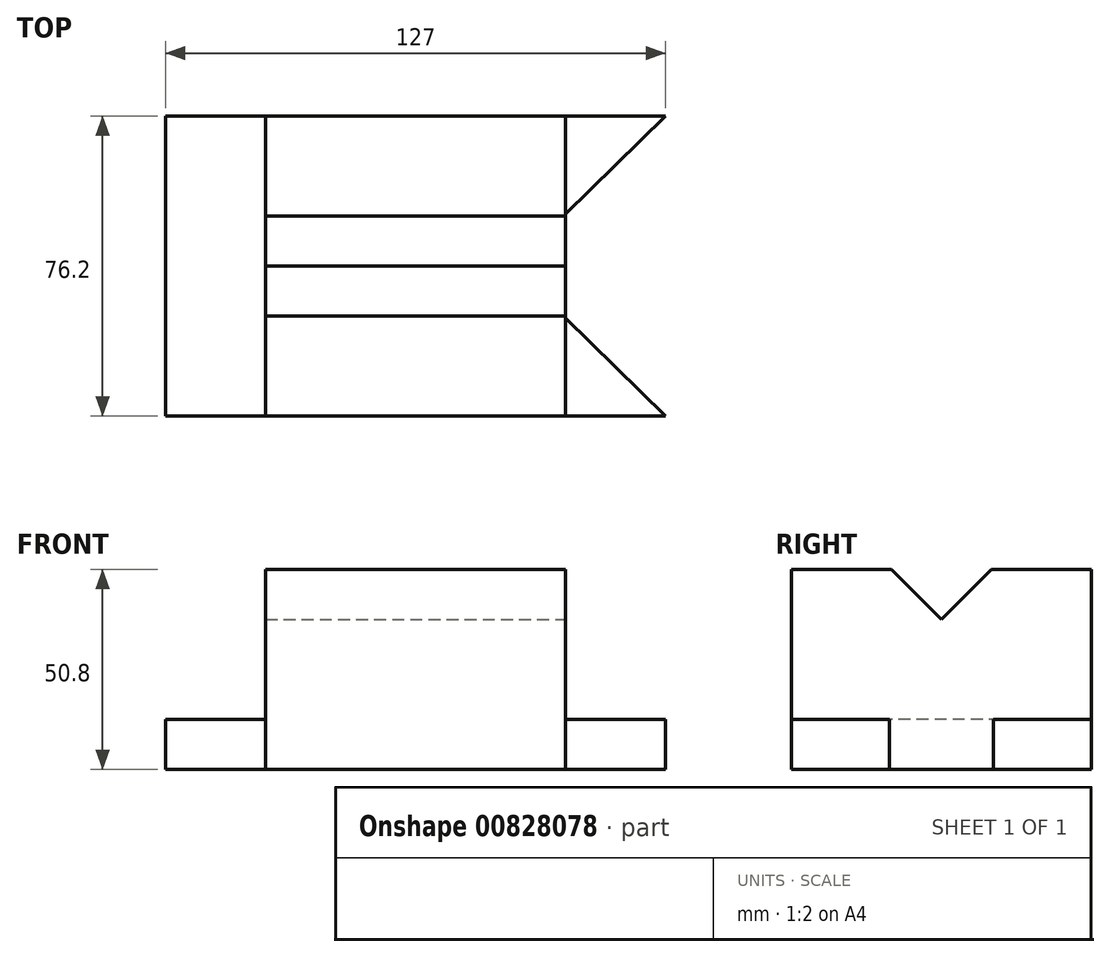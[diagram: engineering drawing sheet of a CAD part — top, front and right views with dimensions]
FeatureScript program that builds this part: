
annotation { "Feature Type Name" : "Feature", "Feature Type Description" : "" }
export const myFeature = defineFeature(function(context is Context, id is Id, definition is map)
    precondition{}
    {
        {
            var Q0;
            Q0=qCreatedBy(makeId("Top.planeOp"),FACE);
            var sketch = newSketch(context, id + "F0", { "sketchPlane" : qUnion([Q0])});
            skLineSegment(sketch, "E0", {"start": v(-30.9, 31.05) * mm, "end": v(-30.9, -45.15) * mm});
            skLineSegment(sketch, "E1", {"start": v(-30.9, -45.15) * mm, "end": v(45.3, -45.15) * mm});
            skLineSegment(sketch, "E2", {"start": v(45.3, -45.15) * mm, "end": v(45.3, -20.23) * mm});
            skLineSegment(sketch, "E3", {"start": v(-30.9, -20.23) * mm, "end": v(-30.9, 6.13) * mm});
            skLineSegment(sketch, "E4", {"start": v(45.3, 6.13) * mm, "end": v(45.3, -20.23) * mm});
            skLineSegment(sketch, "E5", {"start": v(45.3, 6.13) * mm, "end": v(45.3, 31.05) * mm});
            skLineSegment(sketch, "E6", {"start": v(45.3, 31.05) * mm, "end": v(-30.9, 31.05) * mm});
            skLineSegment(sketch, "E7", {"start": v(45.3, 31.05) * mm, "end": v(70.7, 31.05) * mm});
            skLineSegment(sketch, "E8", {"start": v(70.7, 31.05) * mm, "end": v(45.3, 6.13) * mm});
            skLineSegment(sketch, "E9", {"start": v(45.3, -45.15) * mm, "end": v(70.7, -45.15) * mm});
            skLineSegment(sketch, "E10", {"start": v(70.7, -45.15) * mm, "end": v(45.3, -20.23) * mm});
            skLineSegment(sketch, "E11", {"start": v(-30.9, 31.05) * mm, "end": v(-56.3, 31.05) * mm});
            skLineSegment(sketch, "E12", {"start": v(-56.3, 31.05) * mm, "end": v(-56.3, -45.15) * mm});
            skLineSegment(sketch, "E13", {"start": v(-56.3, -45.15) * mm, "end": v(-30.9, -45.15) * mm});
            skSolve(sketch);
        }
        {
            var Q0;
            Q0=makeQuery(id+"F0.imprint","IMPRINT",FACE,{"disambiguationData":[TD([[makeQuery(id+"F0.imprint","IMPRINT",EDGE,{"derivedFrom":sQuery(id+"F0.wireOp",EDGE,"E2")}),-1.0]])]});
            var Q1;
            Q1=makeQuery(id+"F0.imprint","IMPRINT",FACE,{"disambiguationData":[TD([[makeQuery(id+"F0.imprint","IMPRINT",EDGE,{"derivedFrom":sQuery(id+"F0.wireOp",EDGE,"E5")}),-1.0]])]});
            extrude(context, id + "F1", {"entities" : qUnion([Q0, Q1]), "depth" : 12.7 * mm, "offsetDistance" : 25.4 * mm});
        }
        {
            var Q0;
            Q0=makeQuery(id+"F0.imprint","IMPRINT",FACE,{"disambiguationData":[TD([[makeQuery(id+"F0.imprint","IMPRINT",EDGE,{"derivedFrom":sQuery(id+"F0.wireOp",EDGE,"E2")}),-1.0]])]});
            var Q1;
            Q1=makeQuery(id+"F0.imprint","IMPRINT",FACE,{"disambiguationData":[TD([[makeQuery(id+"F0.imprint","IMPRINT",EDGE,{"derivedFrom":sQuery(id+"F0.wireOp",EDGE,"E5")}),-1.0]])]});
            var Q2;
            {var subQ0=sQuery(id+"F0.wireOp",EDGE,"E11");Q2=makeQuery(id+"F0.imprint","IMPRINT",FACE,{"disambiguationData":[TD([[makeQuery(id+"F0.imprint","IMPRINT",EDGE,{"derivedFrom":subQ0}),1.0]])]});}
            extrude(context, id + "F2", {"entities" : qUnion([Q0, Q1, Q2]), "depth" : 12.7 * mm, "offsetDistance" : 25.4 * mm});
        }
        {
            var Q0;
            {var subQ0=sQuery(id+"F0.wireOp",EDGE,"E1");Q0=makeQuery(id+"F0.imprint","IMPRINT",FACE,{"disambiguationData":[TD([[makeQuery(id+"F0.imprint","IMPRINT",EDGE,{"derivedFrom":subQ0}),1.0]])]});}
            extrude(context, id + "F3", {"entities" : qUnion([Q0]), "depth" : 50.8 * mm, "offsetDistance" : 25.4 * mm});
        }
        {
            var Q0;
            Q0=makeQuery(id+"F3.opExtrude","SWEPT_FACE",FACE,{"disambiguationData":[OSD([sQuery(id+"F0.wireOp",EDGE,"E2"),sQuery(id+"F0.wireOp",EDGE,"E4"),sQuery(id+"F0.wireOp",EDGE,"E5")])]});
            var sketch = newSketch(context, id + "F4", { "sketchPlane" : qUnion([Q0])});
            skLineSegment(sketch, "E14", {"start": v(-19.75, 50.8) * mm, "end": v(-7.05, 38.1) * mm});
            skLineSegment(sketch, "E15", {"start": v(-7.05, 38.1) * mm, "end": v(5.65, 50.8) * mm});
            skSolve(sketch);
        }
        {
            var Q0;
            {var subQ0=sQuery(id+"F4.wireOp",EDGE,"E14");Q0=makeQuery(id+"F4.imprint","IMPRINT",FACE,{"disambiguationData":[TD([[makeQuery(id+"F4.imprint","IMPRINT",EDGE,{"derivedFrom":subQ0}),1.0]])]});}
            extrude(context, id + "F5", {"entities" : qUnion([Q0]), "operationType" : NewBodyOperationType.REMOVE, "endBound" : BoundingType.THROUGH_ALL, "oppositeDirection" : true, "depth" : 25.4 * mm, "offsetDistance" : 25.4 * mm});
        }
    });
